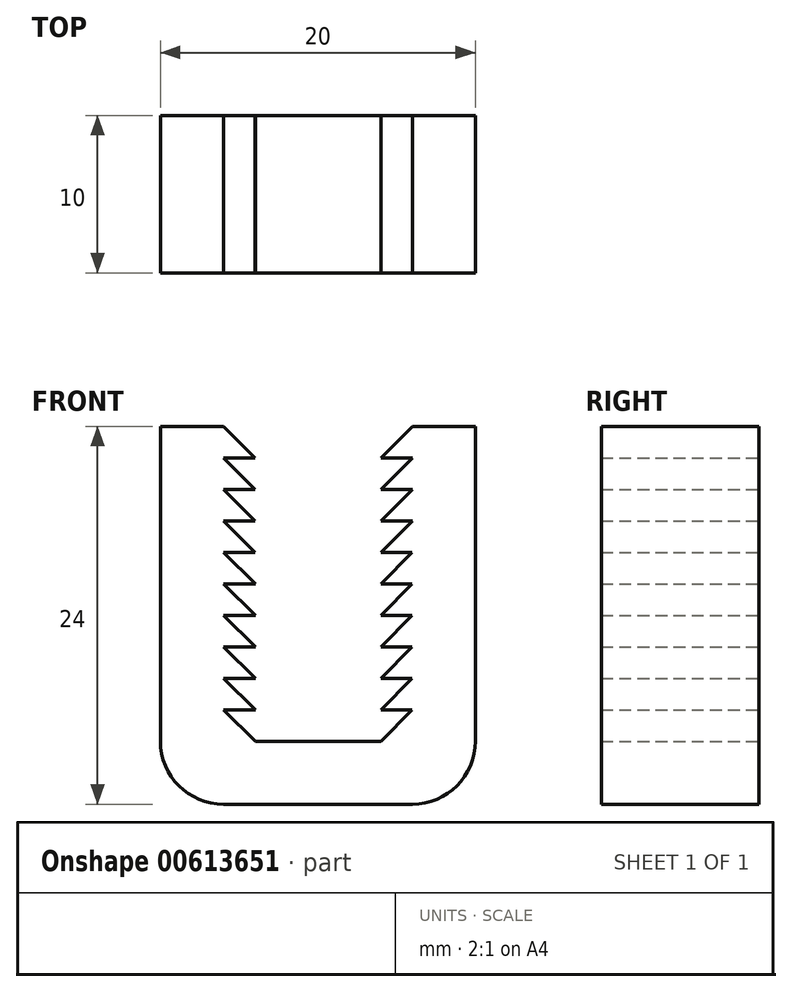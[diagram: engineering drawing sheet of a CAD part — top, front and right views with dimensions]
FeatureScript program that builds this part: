
annotation { "Feature Type Name" : "Feature", "Feature Type Description" : "" }
export const myFeature = defineFeature(function(context is Context, id is Id, definition is map)
    precondition{}
    {
        {
            var Q0;
            Q0=qCreatedBy(makeId("Front.planeOp"),FACE);
            var sketch = newSketch(context, id + "F0", { "sketchPlane" : qUnion([Q0])});
            skLineSegment(sketch, "E0.right", {"start": v(10.5, 0) * mm, "end": v(10.5, 4) * mm});
            skLineSegment(sketch, "E1.top", {"start": v(10.5, 24) * mm, "end": v(6.5, 24) * mm});
            skLineSegment(sketch, "E1.left", {"start": v(10.5, 4) * mm, "end": v(10.5, 24) * mm});
            skLineSegment(sketch, "E2.top", {"start": v(6.5, 22) * mm, "end": v(4.5, 22) * mm});
            skLineSegment(sketch, "E3.bottom", {"start": v(4.5, 22) * mm, "end": v(6.5, 22) * mm});
            skLineSegment(sketch, "E3.top", {"start": v(4.5, 20) * mm, "end": v(6.5, 20) * mm});
            skLineSegment(sketch, "E4.top", {"start": v(4.5, 18) * mm, "end": v(6.5, 18) * mm});
            skLineSegment(sketch, "E5.top", {"start": v(4.5, 16) * mm, "end": v(6.47, 16) * mm});
            skLineSegment(sketch, "E6", {"start": v(6.5, 24) * mm, "end": v(4.5, 22) * mm});
            skLineSegment(sketch, "E7", {"start": v(6.5, 20) * mm, "end": v(4.5, 18) * mm});
            skLineSegment(sketch, "E8", {"start": v(6.5, 22) * mm, "end": v(4.5, 20) * mm});
            skLineSegment(sketch, "E9", {"start": v(6.5, 18) * mm, "end": v(4.5, 16) * mm});
            skLineSegment(sketch, "E10", {"start": v(10.5, 0) * mm, "end": v(0.5, 0) * mm});
            skPoint(sketch, "E11.endSnap0", {"position": v(0.5, 2) * mm});
            skLineSegment(sketch, "E12.MirrorCS", {"start": v(-3.5, 20) * mm, "end": v(-5.5, 20) * mm});
            skLineSegment(sketch, "E13.MirrorCS", {"start": v(-3.5, 18) * mm, "end": v(-5.5, 18) * mm});
            skLineSegment(sketch, "E14.MirrorCS", {"start": v(-5.5, 22) * mm, "end": v(-3.5, 22) * mm});
            skLineSegment(sketch, "E15.MirrorCS", {"start": v(-3.5, 22) * mm, "end": v(-5.5, 22) * mm});
            skLineSegment(sketch, "E16.MirrorCS", {"start": v(-5.5, 20) * mm, "end": v(-3.5, 18) * mm});
            skLineSegment(sketch, "E17.MirrorCS", {"start": v(-5.5, 24) * mm, "end": v(-3.5, 22) * mm});
            skLineSegment(sketch, "E18.MirrorCS", {"start": v(-3.5, 16) * mm, "end": v(-5.47, 16) * mm});
            skLineSegment(sketch, "E19.MirrorCS", {"start": v(-5.5, 22) * mm, "end": v(-3.5, 20) * mm});
            skLineSegment(sketch, "E20.MirrorCS", {"start": v(-9.5, 0) * mm, "end": v(-9.5, 4) * mm});
            skLineSegment(sketch, "E21.MirrorCS", {"start": v(-5.5, 18) * mm, "end": v(-3.5, 16) * mm});
            skLineSegment(sketch, "E22.MirrorCS", {"start": v(-9.5, 0) * mm, "end": v(0.5, 0) * mm});
            skLineSegment(sketch, "E23.MirrorCS", {"start": v(-9.5, 24) * mm, "end": v(-5.5, 24) * mm});
            skLineSegment(sketch, "E24", {"start": v(0.5, -3.5) * mm, "end": v(0.5, -1.09) * mm});
            skLineSegment(sketch, "E25", {"start": v(0.5, -1.09) * mm, "end": v(0.5, 20.25) * mm, "construction": true});
            skLineSegment(sketch, "E26.bottom", {"start": v(-9.5, 0) * mm, "end": v(10.5, 0) * mm});
            skLineSegment(sketch, "E27", {"start": v(-5.47, 14) * mm, "end": v(-3.47, 14) * mm});
            skLineSegment(sketch, "E28", {"start": v(-3.47, 14) * mm, "end": v(-5.47, 16) * mm});
            skLineSegment(sketch, "E29", {"start": v(-5.47, 14) * mm, "end": v(-3.47, 12) * mm});
            skLineSegment(sketch, "E30", {"start": v(-5.47, 12) * mm, "end": v(-3.47, 10) * mm});
            skLineSegment(sketch, "E31", {"start": v(-5.47, 10) * mm, "end": v(-3.47, 8) * mm});
            skLineSegment(sketch, "E32", {"start": v(-5.47, 8) * mm, "end": v(-3.47, 6) * mm});
            skLineSegment(sketch, "E33", {"start": v(-5.47, 6) * mm, "end": v(-3.47, 4) * mm});
            skLineSegment(sketch, "E34", {"start": v(6.47, 14) * mm, "end": v(4.5, 14) * mm});
            skLineSegment(sketch, "E35", {"start": v(6.47, 16) * mm, "end": v(4.5, 14) * mm});
            skLineSegment(sketch, "E36", {"start": v(4.5, 14) * mm, "end": v(6.47, 14) * mm});
            skLineSegment(sketch, "E37", {"start": v(6.47, 14) * mm, "end": v(4.5, 12) * mm});
            skLineSegment(sketch, "E38", {"start": v(6.47, 12) * mm, "end": v(4.5, 10) * mm});
            skLineSegment(sketch, "E39", {"start": v(6.47, 10) * mm, "end": v(4.5, 8) * mm});
            skLineSegment(sketch, "E40", {"start": v(6.47, 8) * mm, "end": v(4.5, 6) * mm});
            skLineSegment(sketch, "E41", {"start": v(6.47, 6) * mm, "end": v(4.5, 4) * mm});
            skLineSegment(sketch, "E42", {"start": v(-3.47, 4) * mm, "end": v(4.5, 4) * mm});
            skLineSegment(sketch, "E43", {"start": v(4.5, 12) * mm, "end": v(6.47, 12) * mm});
            skLineSegment(sketch, "E44", {"start": v(4.5, 10) * mm, "end": v(6.47, 10) * mm});
            skLineSegment(sketch, "E45", {"start": v(4.5, 8) * mm, "end": v(6.47, 8) * mm});
            skLineSegment(sketch, "E46", {"start": v(4.5, 6) * mm, "end": v(6.47, 6) * mm});
            skLineSegment(sketch, "E47", {"start": v(-3.47, 6) * mm, "end": v(-5.47, 6) * mm});
            skLineSegment(sketch, "E48", {"start": v(-3.47, 8) * mm, "end": v(-5.47, 8) * mm});
            skLineSegment(sketch, "E49", {"start": v(-3.47, 10) * mm, "end": v(-5.47, 10) * mm});
            skLineSegment(sketch, "E50", {"start": v(-3.47, 12) * mm, "end": v(-5.47, 12) * mm});
            skLineSegment(sketch, "E51", {"start": v(-9.5, 24) * mm, "end": v(-9.5, 4) * mm});
            skSolve(sketch);
        }
        {
            var Q0;
            Q0=makeQuery(id+"F0.imprint","IMPRINT",FACE,{"disambiguationData":[TD([[makeQuery(id+"F0.imprint","IMPRINT",EDGE,{"derivedFrom":sQuery(id+"F0.wireOp",EDGE,"E1.top")}),1.0]])]});
            extrude(context, id + "F1", {"entities" : qUnion([Q0]), "depth" : 10 * mm, "offsetDistance" : 25 * mm});
        }
        {
            var Q0;
            Q0=makeQuery(id+"F1.opExtrude","SWEPT_EDGE",EDGE,{"disambiguationData":[OSD([sQuery(id+"F0.wireOp",EDGE,"E26.bottom"),sQuery(id+"F0.wireOp",EDGE,"E20.MirrorCS")])]});
            var Q1;
            Q1=makeQuery(id+"F1.opExtrude","SWEPT_EDGE",EDGE,{"disambiguationData":[OSD([sQuery(id+"F0.wireOp",EDGE,"E26.bottom"),sQuery(id+"F0.wireOp",EDGE,"E0.right")])]});
            fillet(context, id + "F2", {"entities" : qUnion([Q0, Q1]), "radius" : 4 * mm, "tangentPropagation" : true, "allowEdgeOverflow" : false});
        }
    });
